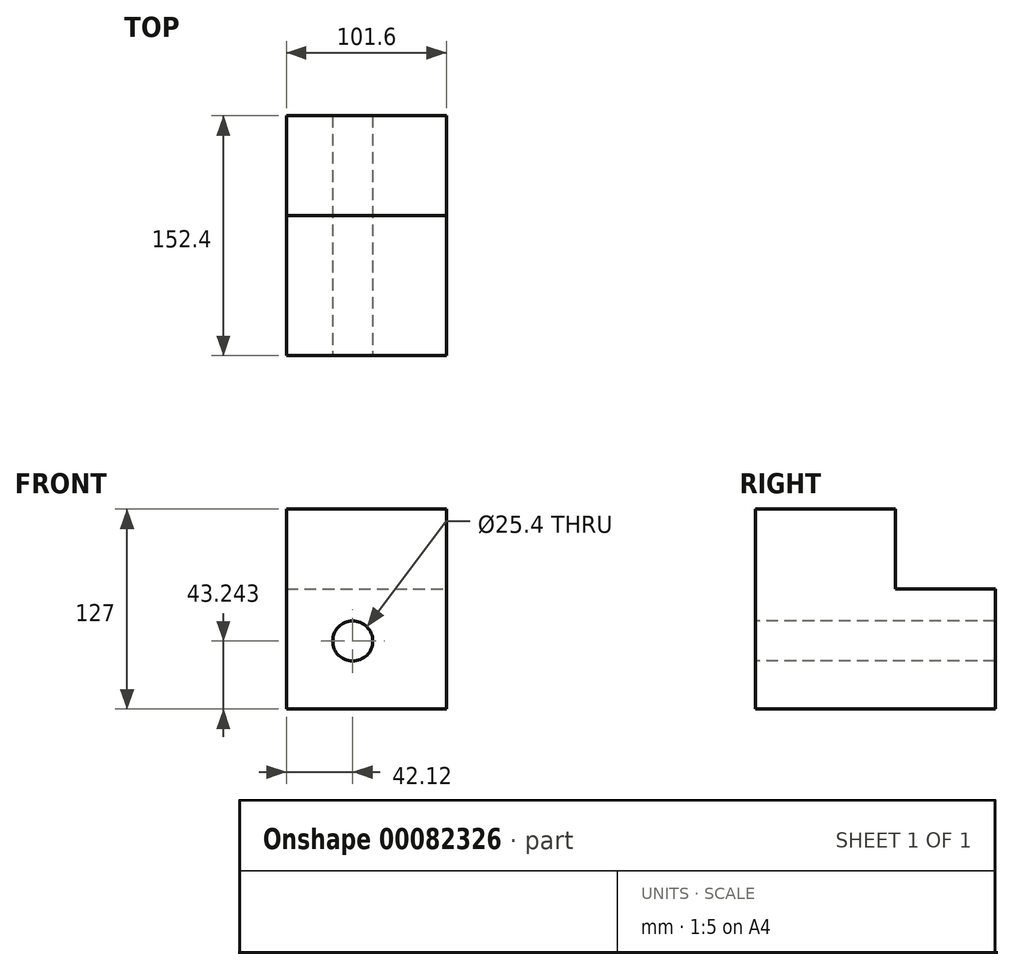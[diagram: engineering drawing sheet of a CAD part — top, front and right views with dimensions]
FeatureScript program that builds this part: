
annotation { "Feature Type Name" : "Feature", "Feature Type Description" : "" }
export const myFeature = defineFeature(function(context is Context, id is Id, definition is map)
    precondition{}
    {
        {
            var Q0;
            Q0=qCreatedBy(makeId("Top.planeOp"),FACE);
            var sketch = newSketch(context, id + "F0", { "sketchPlane" : qUnion([Q0])});
            skLineSegment(sketch, "E0.bottom", {"start": v(-42.12, 114.92) * mm, "end": v(59.48, 114.92) * mm});
            skLineSegment(sketch, "E0.top", {"start": v(-42.12, -37.48) * mm, "end": v(59.48, -37.48) * mm});
            skLineSegment(sketch, "E0.left", {"start": v(-42.12, 114.92) * mm, "end": v(-42.12, -37.48) * mm});
            skLineSegment(sketch, "E0.right", {"start": v(59.48, 114.92) * mm, "end": v(59.48, -37.48) * mm});
            skSolve(sketch);
        }
        {
            var Q0;
            Q0 = qSketchRegion(id + "F0", true);
            extrude(context, id + "F1", {"entities" : qUnion([Q0]), "depth" : 127 * mm});
        }
        {
            var Q0;
            Q0=makeQuery(id+"F1.opExtrude","SWEPT_FACE",FACE,{"disambiguationData":[OSD([sQuery(id+"F0.wireOp",EDGE,"E0.top")])]});
            var sketch = newSketch(context, id + "F2", { "sketchPlane" : qUnion([Q0])});
            skLineSegment(sketch, "E1.bottom", {"start": v(-42.12, 0) * mm, "end": v(0, 0) * mm});
            skLineSegment(sketch, "E1.top", {"start": v(-42.12, 43.24) * mm, "end": v(0, 43.24) * mm});
            skLineSegment(sketch, "E1.left", {"start": v(-42.12, 0) * mm, "end": v(-42.12, 43.24) * mm});
            skLineSegment(sketch, "E1.right", {"start": v(0, 0) * mm, "end": v(0, 43.24) * mm});
            skCircle(sketch, "E2", {"center": v(0, 43.24) * mm, "radius": 12.7 * mm});
            skSolve(sketch);
        }
        {
            var Q0;
            Q0=sQuery(id+"F2.wireOp",VERTEX,"E1.top.end");
            var Q1;
            Q1=makeQuery(id+"F1.opExtrude","SWEPT_BODY",BODY,{"disambiguationData":[OSD([sQuery(id+"F0.wireOp",EDGE,"E0.bottom"),sQuery(id+"F0.wireOp",EDGE,"E0.top"),sQuery(id+"F0.wireOp",EDGE,"E0.left"),sQuery(id+"F0.wireOp",EDGE,"E0.right")])]});
            hole(context, id + "F3", {"style" : HoleStyle.SIMPLE, "endStyle" : HoleEndStyle.THROUGH, "holeDiameter" : 25.4 * mm, "locations" : qUnion([Q0]), "scope" : qUnion([Q1]), "isTappedThrough" : true});
        }
        {
            var Q0;
            Q0=makeQuery(id+"F1.opExtrude","SWEPT_FACE",FACE,{"disambiguationData":[OSD([sQuery(id+"F0.wireOp",EDGE,"E0.right")])]});
            var sketch = newSketch(context, id + "F4", { "sketchPlane" : qUnion([Q0])});
            skLineSegment(sketch, "E3.bottom", {"start": v(114.92, 127) * mm, "end": v(51.42, 127) * mm});
            skLineSegment(sketch, "E3.top", {"start": v(114.92, 76.2) * mm, "end": v(51.42, 76.2) * mm});
            skLineSegment(sketch, "E3.left", {"start": v(114.92, 127) * mm, "end": v(114.92, 76.2) * mm});
            skLineSegment(sketch, "E3.right", {"start": v(51.42, 127) * mm, "end": v(51.42, 76.2) * mm});
            skSolve(sketch);
        }
        {
            var Q0;
            Q0=makeQuery(id+"F4.imprint","IMPRINT",FACE,{"disambiguationData":[TD([[makeQuery(id+"F4.imprint","IMPRINT",EDGE,{"derivedFrom":sQuery(id+"F4.wireOp",EDGE,"E3.bottom")}),1.0]])]});
            var Q1;
            Q1=makeQuery(id+"F1.opExtrude","SWEPT_FACE",FACE,{"disambiguationData":[OSD([sQuery(id+"F0.wireOp",EDGE,"E0.left")])]});
            extrude(context, id + "F5", {"entities" : qUnion([Q0]), "operationType" : NewBodyOperationType.REMOVE, "endBound" : BoundingType.UP_TO_SURFACE, "oppositeDirection" : true, "endBoundEntityFace" : qUnion([Q1]), "depth" : 113.93 * mm});
        }
    });
